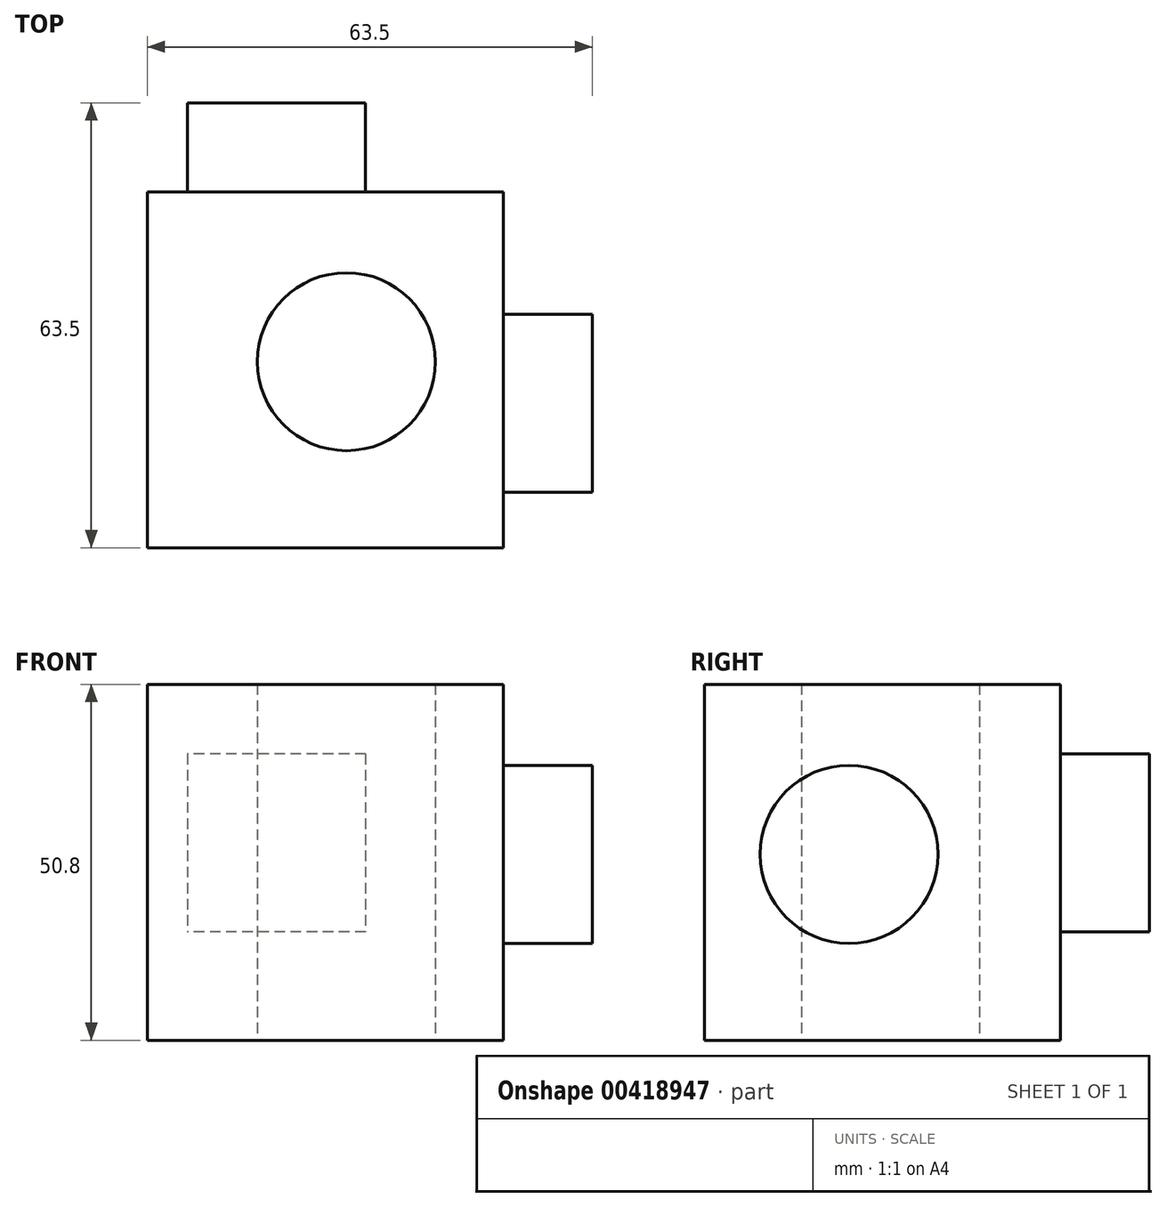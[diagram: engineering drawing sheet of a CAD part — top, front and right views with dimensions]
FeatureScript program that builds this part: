
annotation { "Feature Type Name" : "Feature", "Feature Type Description" : "" }
export const myFeature = defineFeature(function(context is Context, id is Id, definition is map)
    precondition{}
    {
        {
            var Q0;
            Q0=qCreatedBy(makeId("Front.planeOp"),FACE);
            var sketch = newSketch(context, id + "F0", { "sketchPlane" : qUnion([Q0])});
            skLineSegment(sketch, "E0.bottom", {"start": v(-31.13, 9.94) * mm, "end": v(19.67, 9.94) * mm});
            skLineSegment(sketch, "E0.top", {"start": v(-31.13, -40.86) * mm, "end": v(19.67, -40.86) * mm});
            skLineSegment(sketch, "E0.left", {"start": v(-31.13, 9.94) * mm, "end": v(-31.13, -40.86) * mm});
            skLineSegment(sketch, "E0.right", {"start": v(19.67, 9.94) * mm, "end": v(19.67, -40.86) * mm});
            skSolve(sketch);
        }
        {
            var Q0;
            Q0 = qSketchRegion(id + "F0", true);
            extrude(context, id + "F1", {"entities" : qUnion([Q0]), "depth" : 50.8 * mm});
        }
        {
            var Q0;
            Q0=makeQuery(id+"F1.opExtrude","SWEPT_FACE",FACE,{"disambiguationData":[OSD([sQuery(id+"F0.wireOp",EDGE,"E0.right")])]});
            var sketch = newSketch(context, id + "F2", { "sketchPlane" : qUnion([Q0])});
            skCircle(sketch, "E1", {"center": v(-30.17, -14.32) * mm, "radius": 12.7 * mm});
            skSolve(sketch);
        }
        {
            var Q0;
            Q0 = qSketchRegion(id + "F2", true);
            extrude(context, id + "F3", {"entities" : qUnion([Q0]), "operationType" : NewBodyOperationType.ADD, "depth" : 12.7 * mm});
        }
        {
            var Q0;
            Q0=makeQuery(id+"F1.opExtrude","CAP_FACE",FACE,{"disambiguationData":[OSD([sQuery(id+"F0.wireOp",EDGE,"E0.bottom"),sQuery(id+"F0.wireOp",EDGE,"E0.top"),sQuery(id+"F0.wireOp",EDGE,"E0.left"),sQuery(id+"F0.wireOp",EDGE,"E0.right")])],"isStart":true});
            var sketch = newSketch(context, id + "F4", { "sketchPlane" : qUnion([Q0])});
            skLineSegment(sketch, "E2.bottom", {"start": v(0, 0) * mm, "end": v(25.4, 0) * mm});
            skLineSegment(sketch, "E2.top", {"start": v(0, -25.4) * mm, "end": v(25.4, -25.4) * mm});
            skLineSegment(sketch, "E2.left", {"start": v(0, 0) * mm, "end": v(0, -25.4) * mm});
            skLineSegment(sketch, "E2.right", {"start": v(25.4, 0) * mm, "end": v(25.4, -25.4) * mm});
            skSolve(sketch);
        }
        {
            var Q0;
            Q0 = qSketchRegion(id + "F4", true);
            extrude(context, id + "F5", {"entities" : qUnion([Q0]), "operationType" : NewBodyOperationType.ADD, "depth" : 12.7 * mm});
        }
        {
            var Q0;
            Q0=makeQuery(id+"F1.opExtrude","SWEPT_FACE",FACE,{"disambiguationData":[OSD([sQuery(id+"F0.wireOp",EDGE,"E0.top")])]});
            var sketch = newSketch(context, id + "F6", { "sketchPlane" : qUnion([Q0])});
            skCircle(sketch, "E3", {"center": v(-2.73, 24.26) * mm, "radius": 12.7 * mm});
            skSolve(sketch);
        }
        {
            var Q0;
            Q0 = qSketchRegion(id + "F6", true);
            extrude(context, id + "F7", {"entities" : qUnion([Q0]), "operationType" : NewBodyOperationType.REMOVE, "oppositeDirection" : true, "depth" : 50.8 * mm});
        }
    });
